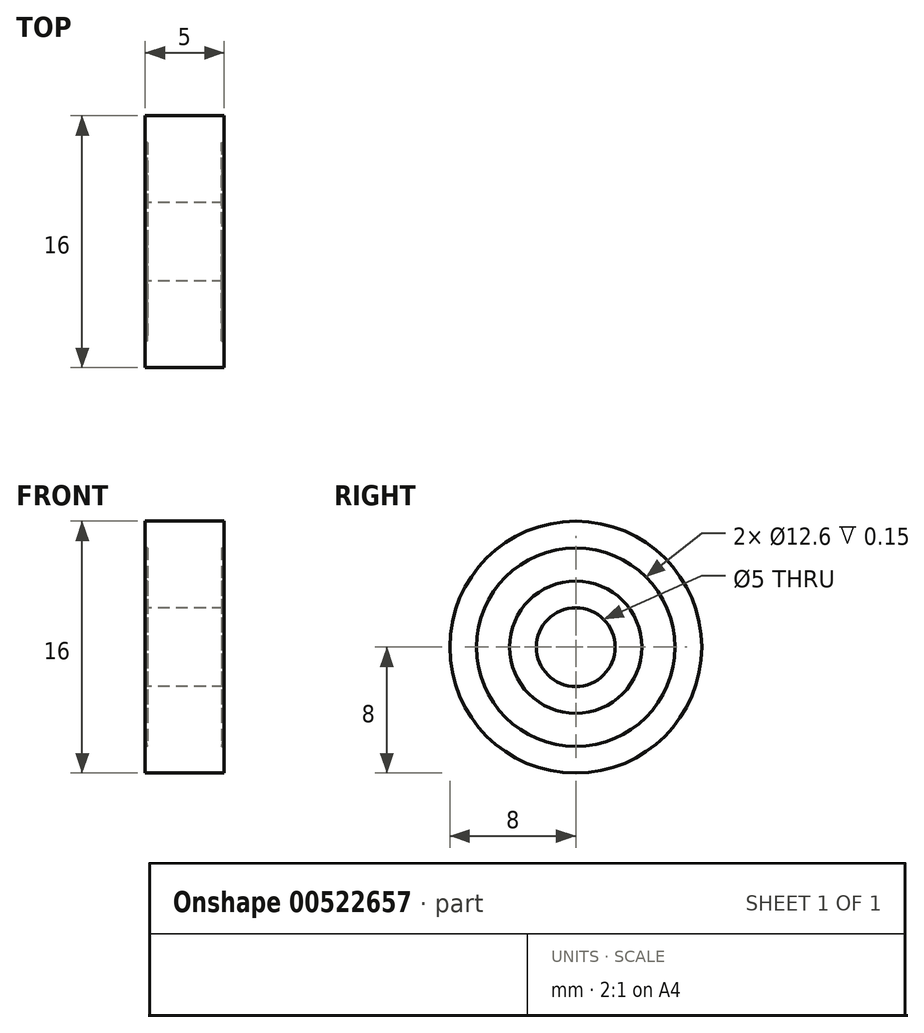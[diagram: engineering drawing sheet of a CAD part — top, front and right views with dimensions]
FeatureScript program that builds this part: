
annotation { "Feature Type Name" : "Feature", "Feature Type Description" : "" }
export const myFeature = defineFeature(function(context is Context, id is Id, definition is map)
    precondition{}
    {
        {
            var Q0;
            Q0=qCreatedBy(makeId("Front.planeOp"),FACE);
            var sketch = newSketch(context, id + "F0", { "sketchPlane" : qUnion([Q0])});
            skLineSegment(sketch, "E0", {"start": v(-17.4, 0) * mm, "end": v(25.76, 0) * mm, "construction": true});
            skLineSegment(sketch, "E1", {"start": v(0, 2.5) * mm, "end": v(-2.5, 2.5) * mm});
            skLineSegment(sketch, "E2", {"start": v(-2.5, 2.5) * mm, "end": v(-2.5, 4.2) * mm});
            skLineSegment(sketch, "E3", {"start": v(-2.5, 4.2) * mm, "end": v(-2.35, 4.2) * mm});
            skLineSegment(sketch, "E4", {"start": v(-2.35, 6.3) * mm, "end": v(-2.5, 6.3) * mm});
            skLineSegment(sketch, "E5", {"start": v(-2.5, 6.3) * mm, "end": v(-2.5, 8) * mm});
            skLineSegment(sketch, "E6", {"start": v(-2.5, 8) * mm, "end": v(0, 8) * mm});
            skLineSegment(sketch, "E7", {"start": v(0, 8) * mm, "end": v(0, 2.5) * mm});
            skArc(sketch, "E8", {"start": v(-2.35, 6.3) * mm, "mid": v(-2.5, 5.25) * mm, "end": v(-2.35, 4.2) * mm});
            skLineSegment(sketch, "E9", {"start": v(0, -15.75) * mm, "end": v(0, 21.22) * mm, "construction": true});
            skPoint(sketch, "E10", {"position": v(0, 5.25) * mm});
            skSolve(sketch);
        }
        {
            var Q0;
            Q0=qSketchRegion(id+"F0",true);
            var Q1;
            Q1=sQuery(id+"F0.wireOp",EDGE,"E0");
            revolve(context, id + "F1", {"entities" : qUnion([Q0]), "axis" : qUnion([Q1]), "revolveType" : RevolveType.FULL});
        }
        {
            var Q0;
            Q0=makeQuery(id+"F1.opRevolve","SWEPT_BODY",BODY,{"disambiguationData":[OSD([sQuery(id+"F0.wireOp",EDGE,"E1"),sQuery(id+"F0.wireOp",EDGE,"E2"),sQuery(id+"F0.wireOp",EDGE,"E3"),sQuery(id+"F0.wireOp",EDGE,"E4"),sQuery(id+"F0.wireOp",EDGE,"E5"),sQuery(id+"F0.wireOp",EDGE,"E6"),sQuery(id+"F0.wireOp",EDGE,"E7"),sQuery(id+"F0.wireOp",EDGE,"E8")])]});
            var Q1;
            Q1=qCreatedBy(makeId("Right.planeOp"),FACE);
            mirror(context, id + "F2", {"operationType" : NewBodyOperationType.ADD, "entities" : qUnion([Q0]), "mirrorPlane" : qUnion([Q1])});
        }
    });
